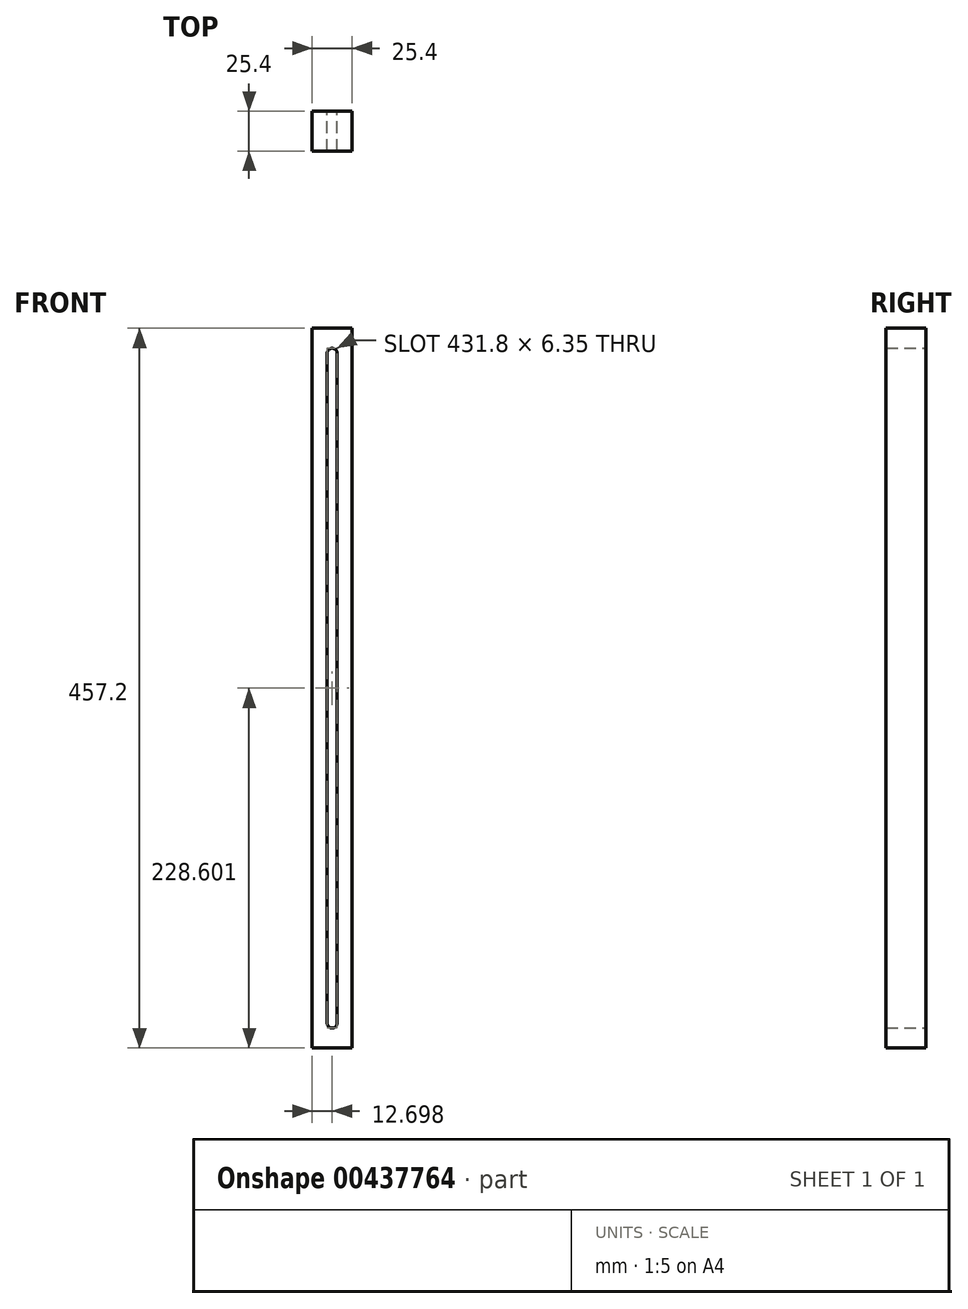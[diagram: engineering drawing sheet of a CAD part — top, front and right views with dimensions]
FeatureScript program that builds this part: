
annotation { "Feature Type Name" : "Feature", "Feature Type Description" : "" }
export const myFeature = defineFeature(function(context is Context, id is Id, definition is map)
    precondition{}
    {
        {
            var Q0;
            Q0=qCreatedBy(makeId("Front.planeOp"),FACE);
            var sketch = newSketch(context, id + "F0", { "sketchPlane" : qUnion([Q0])});
            skLineSegment(sketch, "E0.bottom", {"start": v(25.12, 221.8) * mm, "end": v(-0.28, 221.8) * mm});
            skLineSegment(sketch, "E0.top", {"start": v(25.12, -235.4) * mm, "end": v(-0.28, -235.4) * mm});
            skLineSegment(sketch, "E0.left", {"start": v(25.12, 221.8) * mm, "end": v(25.12, -235.4) * mm});
            skLineSegment(sketch, "E0.right", {"start": v(-0.28, 221.8) * mm, "end": v(-0.28, -235.4) * mm});
            skArc(sketch, "E1", {"start": v(15.6, 205.93) * mm, "mid": v(12.42, 209.1) * mm, "end": v(9.24, 205.93) * mm});
            skArc(sketch, "E2", {"start": v(9.24, -219.52) * mm, "mid": v(12.42, -222.7) * mm, "end": v(15.6, -219.52) * mm});
            skPoint(sketch, "E2.centerSnap0", {"position": v(12.42, -235.4) * mm});
            skLineSegment(sketch, "E3", {"start": v(15.6, 205.93) * mm, "end": v(15.6, -219.52) * mm});
            skLineSegment(sketch, "E4", {"start": v(9.24, -219.52) * mm, "end": v(9.24, 205.93) * mm});
            skSolve(sketch);
        }
        {
            var Q0;
            Q0 = qSketchRegion(id + "F0", true);
            extrude(context, id + "F1", {"entities" : qUnion([Q0]), "depth" : 25.4 * mm, "offsetDistance" : 25.4 * mm});
        }
    });
